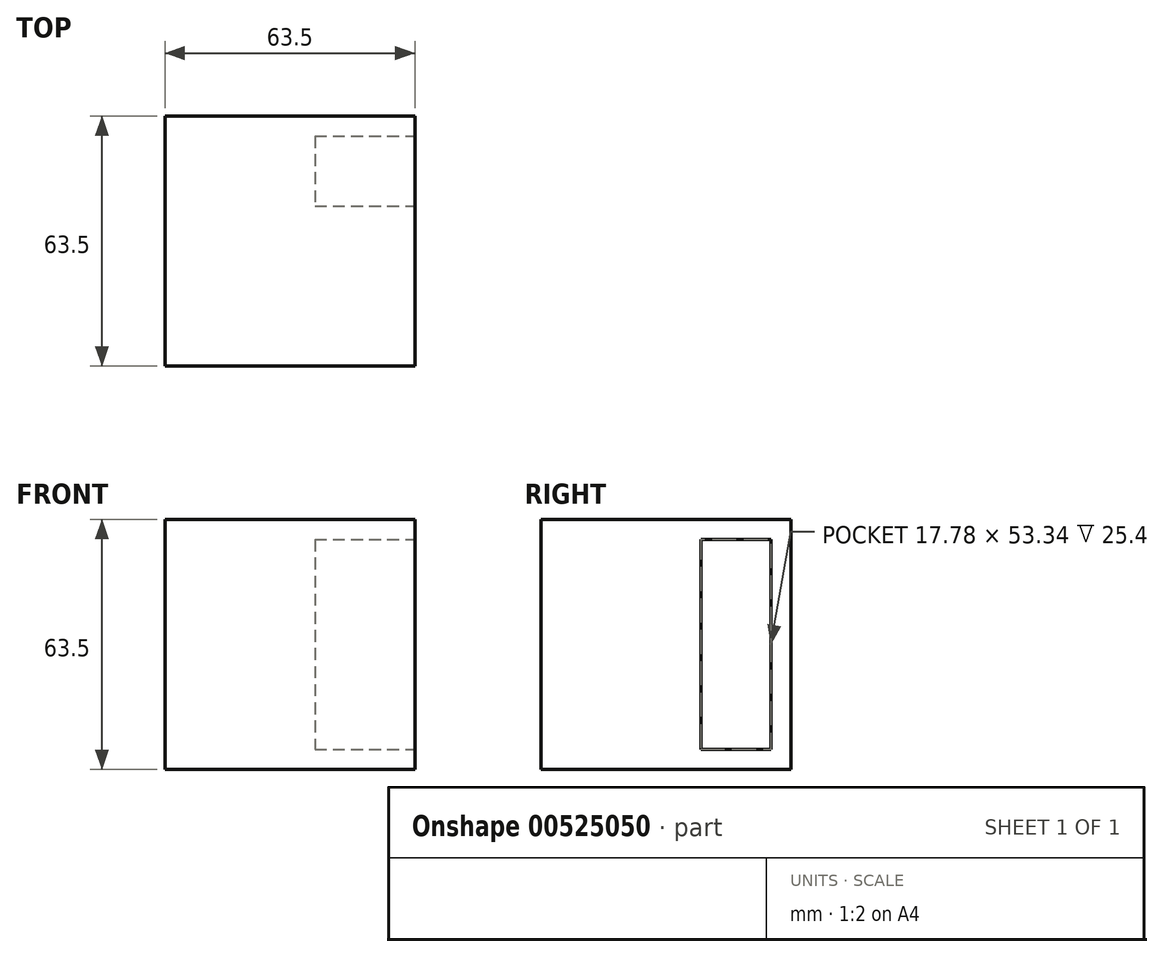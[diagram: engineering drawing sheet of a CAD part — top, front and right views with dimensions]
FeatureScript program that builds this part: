
annotation { "Feature Type Name" : "Feature", "Feature Type Description" : "" }
export const myFeature = defineFeature(function(context is Context, id is Id, definition is map)
    precondition{}
    {
        {
            var Q0;
            Q0=qCreatedBy(makeId("Top.planeOp"),FACE);
            var sketch = newSketch(context, id + "F0", { "sketchPlane" : qUnion([Q0])});
            skLineSegment(sketch, "E0.bottom", {"start": v(31.75, 31.75) * mm, "end": v(-31.75, 31.75) * mm});
            skLineSegment(sketch, "E0.top", {"start": v(31.75, -31.75) * mm, "end": v(-31.75, -31.75) * mm});
            skLineSegment(sketch, "E0.left", {"start": v(31.75, 31.75) * mm, "end": v(31.75, -31.75) * mm});
            skLineSegment(sketch, "E0.right", {"start": v(-31.75, 31.75) * mm, "end": v(-31.75, -31.75) * mm});
            skPoint(sketch, "E0.middle", {"position": v(0, 0) * mm});
            skSolve(sketch);
        }
        {
            var Q0;
            Q0=makeQuery(id+"F0.imprint","IMPRINT",FACE,{"disambiguationData":[TD([[makeQuery(id+"F0.imprint","IMPRINT",EDGE,{"derivedFrom":sQuery(id+"F0.wireOp",EDGE,"E0.bottom")}),1.0]])]});
            extrude(context, id + "F1", {"entities" : qUnion([Q0]), "depth" : 63.5 * mm, "offsetDistance" : 25.4 * mm});
        }
        {
            var Q0;
            Q0=makeQuery(id+"F1.opExtrude","SWEPT_FACE",FACE,{"disambiguationData":[OSD([sQuery(id+"F0.wireOp",EDGE,"E0.left")])]});
            var sketch = newSketch(context, id + "F2", { "sketchPlane" : qUnion([Q0])});
            skLineSegment(sketch, "E1.bottom", {"start": v(-26.67, 58.42) * mm, "end": v(-8.89, 58.42) * mm});
            skLineSegment(sketch, "E1.top", {"start": v(-26.67, 5.08) * mm, "end": v(-8.89, 5.08) * mm});
            skLineSegment(sketch, "E1.left", {"start": v(-26.67, 58.42) * mm, "end": v(-26.67, 5.08) * mm});
            skLineSegment(sketch, "E1.right", {"start": v(-8.89, 58.42) * mm, "end": v(-8.89, 5.08) * mm});
            skLineSegment(sketch, "E2.MirrorCS", {"start": v(26.67, 58.42) * mm, "end": v(8.9, 58.42) * mm});
            skLineSegment(sketch, "E3.MirrorCS", {"start": v(26.67, 58.42) * mm, "end": v(26.67, 5.08) * mm});
            skLineSegment(sketch, "E4.MirrorCS", {"start": v(8.9, 58.42) * mm, "end": v(8.9, 5.08) * mm});
            skLineSegment(sketch, "E5.MirrorCS", {"start": v(26.67, 5.08) * mm, "end": v(8.9, 5.08) * mm});
            skSolve(sketch);
        }
        {
            var Q0;
            Q0=makeQuery(id+"F2.imprint","IMPRINT",FACE,{"disambiguationData":[TD([[makeQuery(id+"F2.imprint","IMPRINT",EDGE,{"derivedFrom":sQuery(id+"F2.wireOp",EDGE,"E2.MirrorCS")}),1.0]])]});
            extrude(context, id + "F3", {"entities" : qUnion([Q0]), "operationType" : NewBodyOperationType.REMOVE, "oppositeDirection" : true, "depth" : 25.4 * mm, "offsetDistance" : 25.4 * mm});
        }
    });
